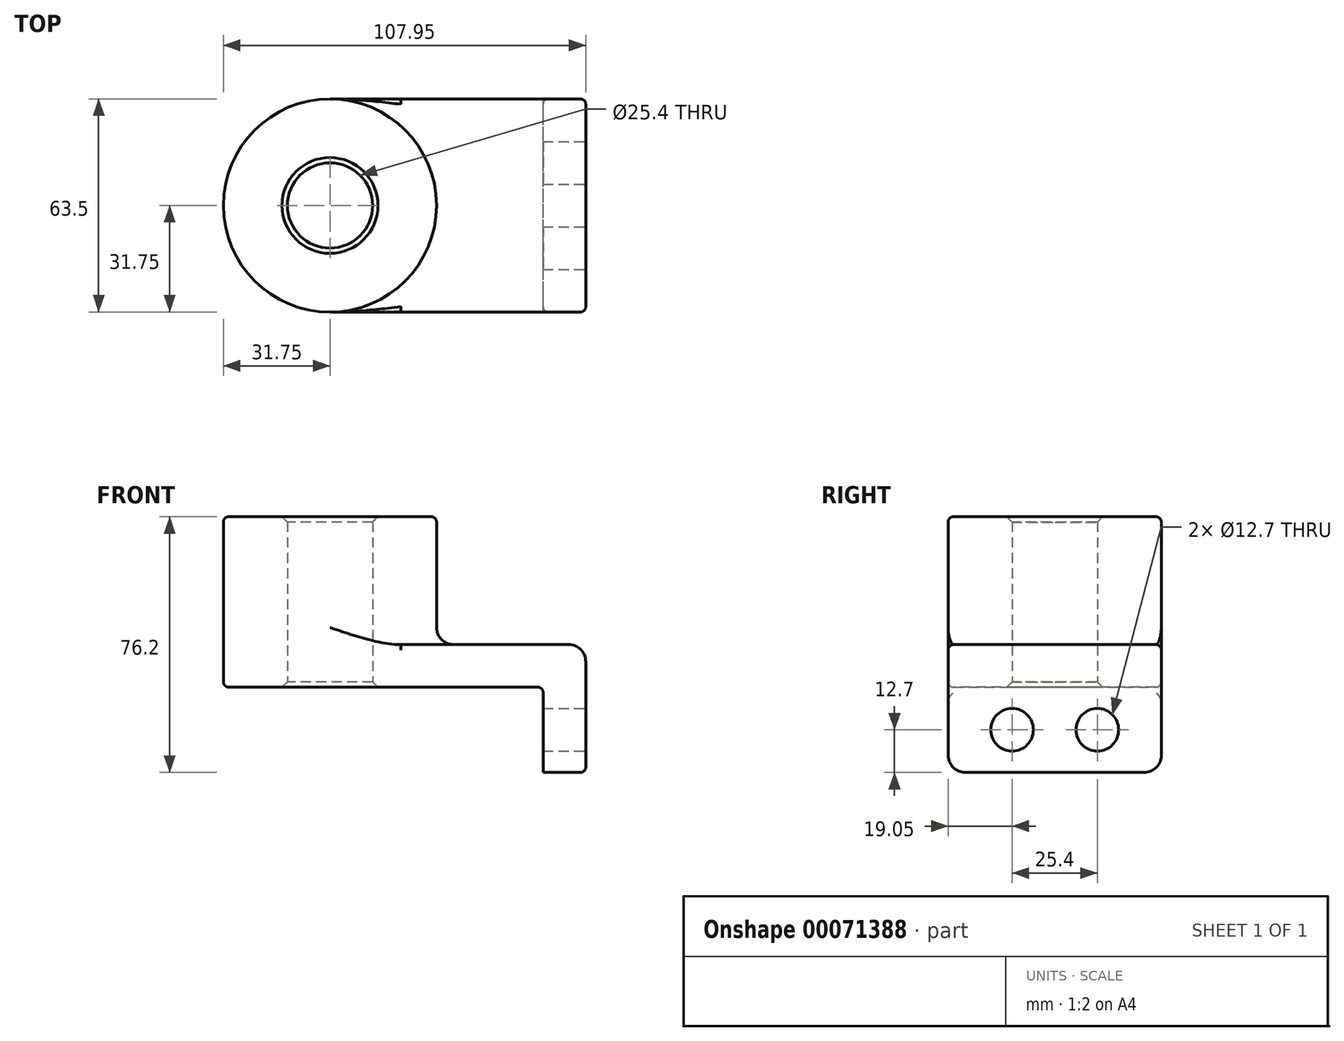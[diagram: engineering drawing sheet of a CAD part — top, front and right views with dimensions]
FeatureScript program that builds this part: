
annotation { "Feature Type Name" : "Feature", "Feature Type Description" : "" }
export const myFeature = defineFeature(function(context is Context, id is Id, definition is map)
    precondition{}
    {
        {
            var Q0;
            Q0=qCreatedBy(makeId("Top.planeOp"),FACE);
            var sketch = newSketch(context, id + "F0", { "sketchPlane" : qUnion([Q0])});
            skLineSegment(sketch, "E0.rect.bottom", {"start": v(38.1, -31.75) * mm, "end": v(-38.1, -31.75) * mm});
            skLineSegment(sketch, "E0.rect.top", {"start": v(38.1, 31.75) * mm, "end": v(-38.1, 31.75) * mm});
            skLineSegment(sketch, "E0.rect.left", {"start": v(38.1, -31.75) * mm, "end": v(38.1, 31.75) * mm});
            skLineSegment(sketch, "E0.rect.right", {"start": v(-38.1, -31.75) * mm, "end": v(-38.1, 31.75) * mm});
            skPoint(sketch, "E0.rect.middle", {"position": v(0, 0) * mm});
            skCircle(sketch, "E1", {"center": v(-38.1, 0) * mm, "radius": 31.75 * mm});
            skCircle(sketch, "E2", {"center": v(-38.1, 0) * mm, "radius": 12.7 * mm});
            skSolve(sketch);
        }
        {
            var Q0;
            Q0 = qSketchRegion(id + "F0", true);
            extrude(context, id + "F1", {"entities" : qUnion([Q0]), "depth" : 12.7 * mm});
        }
        {
            var Q0;
            {var subQ1=sQuery(id+"F0.wireOp",EDGE,"E0.rect.right");var subQ3=sQuery(id+"F0.wireOp",EDGE,"E2");var subQ4=makeQuery(id+"F0.imprint","INTERSECT",VERTEX,{"disambiguationData":[OD(0.0)],"derivedFrom":[subQ1,subQ3]});Q0=makeQuery(id+"F0.imprint","IMPRINT",FACE,{"disambiguationData":[TD([[makeQuery(id+"F0.imprint","IMPRINT",EDGE,{"disambiguationData":[TD([[subQ4,1.0]])],"derivedFrom":subQ3}),-1.0]])]});}
            var Q1;
            {var subQ1=sQuery(id+"F0.wireOp",EDGE,"E0.rect.right");var subQ3=sQuery(id+"F0.wireOp",EDGE,"E2");var subQ4=makeQuery(id+"F0.imprint","INTERSECT",VERTEX,{"disambiguationData":[OD(0.0)],"derivedFrom":[subQ1,subQ3]});Q1=makeQuery(id+"F0.imprint","IMPRINT",FACE,{"disambiguationData":[TD([[makeQuery(id+"F0.imprint","IMPRINT",EDGE,{"disambiguationData":[TD([[subQ4,-1.0]])],"derivedFrom":subQ3}),-1.0]])]});}
            extrude(context, id + "F2", {"entities" : qUnion([Q0, Q1]), "operationType" : NewBodyOperationType.ADD, "depth" : 50.8 * mm});
        }
        {
            var Q0;
            Q0=makeQuery(id+"F1.opExtrude","SWEPT_FACE",FACE,{"disambiguationData":[OSD([sQuery(id+"F0.wireOp",EDGE,"E0.rect.left")])]});
            var sketch = newSketch(context, id + "F3", { "sketchPlane" : qUnion([Q0])});
            skLineSegment(sketch, "E3.bottom", {"start": v(-31.75, 12.7) * mm, "end": v(31.75, 12.7) * mm});
            skLineSegment(sketch, "E3.top", {"start": v(-31.75, -25.4) * mm, "end": v(31.75, -25.4) * mm});
            skLineSegment(sketch, "E3.left", {"start": v(-31.75, 12.7) * mm, "end": v(-31.75, -25.4) * mm});
            skLineSegment(sketch, "E3.right", {"start": v(31.75, 12.7) * mm, "end": v(31.75, -25.4) * mm});
            skCircle(sketch, "E4", {"center": v(-12.7, -12.7) * mm, "radius": 6.35 * mm});
            skLineSegment(sketch, "E5", {"start": v(0, 0) * mm, "end": v(0, -25.4) * mm, "construction": true});
            skCircle(sketch, "E6.MirrorC", {"center": v(12.7, -12.7) * mm, "radius": 6.35 * mm});
            skSolve(sketch);
        }
        {
            var Q0;
            Q0 = qSketchRegion(id + "F3", true);
            extrude(context, id + "F4", {"entities" : qUnion([Q0]), "operationType" : NewBodyOperationType.ADD, "oppositeDirection" : true, "depth" : 12.7 * mm});
        }
        {
            var Q0;
            {var subQ0=sQuery(id+"F0.wireOp",EDGE,"E1");Q0=makeQuery(id+"F2.boolean.opBoolean","INTERSECT",EDGE,{"derivedFrom":[makeQuery(id+"F1.opExtrude","CAP_FACE",FACE,{"disambiguationData":[OSD([sQuery(id+"F0.wireOp",EDGE,"E0.rect.bottom"),sQuery(id+"F0.wireOp",EDGE,"E0.rect.top"),sQuery(id+"F0.wireOp",EDGE,"E0.rect.left"),subQ0,sQuery(id+"F0.wireOp",EDGE,"E2")])],"isStart":false}),makeQuery(id+"F2.opExtrude","SWEPT_FACE",FACE,{"disambiguationData":[OSD([subQ0])]})]});}
            var Q1;
            Q1=makeQuery(id+"F1.opExtrude","CAP_EDGE",EDGE,{"disambiguationData":[OSD([sQuery(id+"F0.wireOp",EDGE,"E0.rect.left")])],"isStart":false});
            var Q2;
            Q2=makeQuery(id+"F4.opExtrude","SWEPT_EDGE",EDGE,{"disambiguationData":[OSD([sQuery(id+"F3.wireOp",EDGE,"E3.top"),sQuery(id+"F3.wireOp",EDGE,"E3.left")])]});
            var Q3;
            Q3=makeQuery(id+"F4.opExtrude","SWEPT_EDGE",EDGE,{"disambiguationData":[OSD([sQuery(id+"F3.wireOp",EDGE,"E3.top"),sQuery(id+"F3.wireOp",EDGE,"E3.right")])]});
            fillet(context, id + "F5", {"entities" : qUnion([Q0, Q1, Q2, Q3]), "radius" : 5.08 * mm, "tangentPropagation" : true, "allowEdgeOverflow" : false});
        }
        {
            var Q0;
            Q0=makeQuery(id+"F1.opExtrude","CAP_EDGE",EDGE,{"disambiguationData":[OSD([sQuery(id+"F0.wireOp",EDGE,"E0.rect.bottom")])],"isStart":false});
            var Q1;
            Q1=makeQuery(id+"F1.opExtrude","CAP_EDGE",EDGE,{"disambiguationData":[OSD([sQuery(id+"F0.wireOp",EDGE,"E0.rect.bottom")])],"isStart":true});
            var Q2;
            Q2=makeQuery(id+"F4.boolean.opBoolean","INTERSECT",EDGE,{"derivedFrom":[makeQuery(id+"F1.opExtrude","CAP_FACE",FACE,{"disambiguationData":[OSD([sQuery(id+"F0.wireOp",EDGE,"E0.rect.bottom"),sQuery(id+"F0.wireOp",EDGE,"E0.rect.top"),sQuery(id+"F0.wireOp",EDGE,"E0.rect.left"),sQuery(id+"F0.wireOp",EDGE,"E1"),sQuery(id+"F0.wireOp",EDGE,"E2")])],"isStart":true}),makeQuery(id+"F4.opExtrude","CAP_FACE",FACE,{"disambiguationData":[OSD([sQuery(id+"F3.wireOp",EDGE,"E3.bottom"),sQuery(id+"F3.wireOp",EDGE,"E3.top"),sQuery(id+"F3.wireOp",EDGE,"E3.left"),sQuery(id+"F3.wireOp",EDGE,"E3.right"),sQuery(id+"F3.wireOp",EDGE,"E4"),sQuery(id+"F3.wireOp",EDGE,"E6.MirrorC")])],"isStart":false})]});
            var Q3;
            Q3=makeQuery(id+"F2.opExtrude","CAP_EDGE",EDGE,{"disambiguationData":[OSD([sQuery(id+"F0.wireOp",EDGE,"E1")])],"isStart":false});
            fillet(context, id + "F6", {"entities" : qUnion([Q0, Q1, Q2, Q3]), "radius" : 1.59 * mm, "tangentPropagation" : true, "allowEdgeOverflow" : false});
        }
        {
            var Q0;
            {var subQ0=sQuery(id+"F0.wireOp",EDGE,"E2");Q0=makeQuery(id+"F2.boolean.opBoolean","MERGE",FACE,{"derivedFrom":[makeQuery(id+"F1.opExtrude","SWEPT_FACE",FACE,{"disambiguationData":[OSD([subQ0])]}),makeQuery(id+"F2.opExtrude","SWEPT_FACE",FACE,{"disambiguationData":[OSD([subQ0])]})]});}
            chamfer(context, id + "F7", {"entities" : qUnion([Q0]), "width" : 1.59 * mm, "tangentPropagation" : true});
        }
    });
